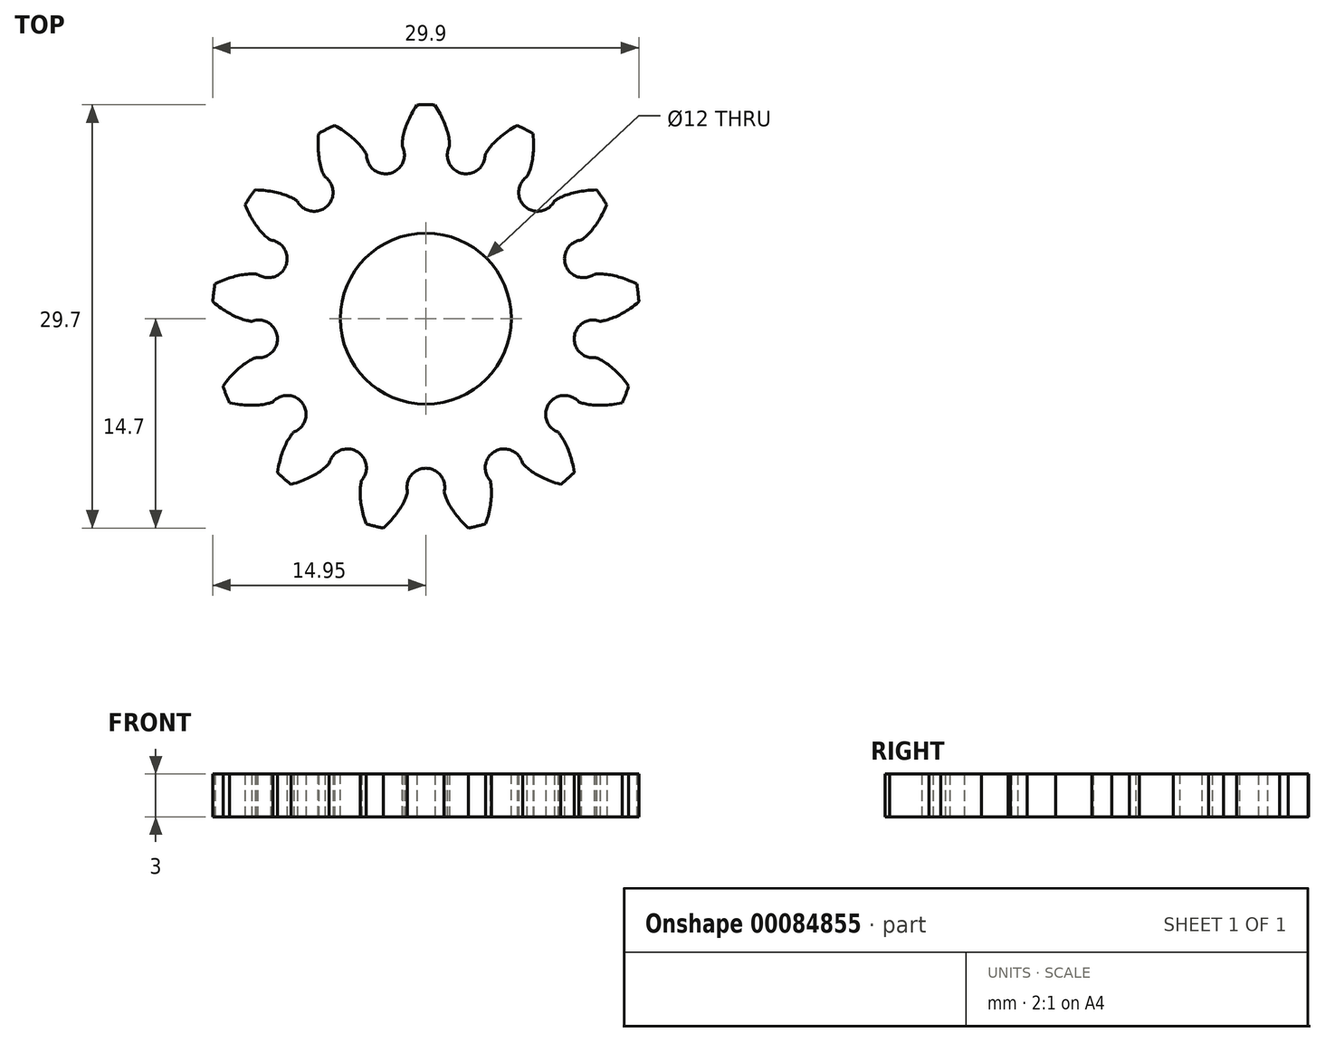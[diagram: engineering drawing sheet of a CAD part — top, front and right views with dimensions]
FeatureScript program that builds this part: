
annotation { "Feature Type Name" : "Feature", "Feature Type Description" : "" }
export const myFeature = defineFeature(function(context is Context, id is Id, definition is map)
    precondition{}
    {
        {
            assignVariable(context, id + "F0", {"name" : "Z", "anyValue" : 13});
        }
        {
            assignVariable(context, id + "F1", {"name" : "e", "anyValue" : 3});
        }
        {
            var Q0;
            Q0=qCreatedBy(makeId("Top.planeOp"),FACE);
            var sketch = newSketch(context, id + "F2", { "sketchPlane" : qUnion([Q0])});
            skCircle(sketch, "E0", {"center": v(0, 0) * mm, "radius": 13 * mm, "construction": true});
            skCircle(sketch, "E1", {"center": v(0, 0) * mm, "radius": 15 * mm, "construction": true});
            skLineSegment(sketch, "E2", {"start": v(-8.95, 13) * mm, "end": v(8.95, 13) * mm, "construction": true});
            skLineSegment(sketch, "E3", {"start": v(0, 0) * mm, "end": v(0, 13) * mm, "construction": true});
            skLineSegment(sketch, "E4", {"start": v(-4.18, 11.48) * mm, "end": v(0, 13) * mm, "construction": true});
            skLineSegment(sketch, "E5", {"start": v(0, 0) * mm, "end": v(-4.18, 11.48) * mm, "construction": true});
            skCircle(sketch, "E6", {"center": v(0, 0) * mm, "radius": 12.22 * mm, "construction": true});
            skLineSegment(sketch, "E7", {"start": v(-1.66, 12.1) * mm, "end": v(0.52, 12.2) * mm, "construction": true});
            skLineSegment(sketch, "E8", {"start": v(0.52, 12.2) * mm, "end": v(2.67, 11.92) * mm, "construction": true});
            skLineSegment(sketch, "E9", {"start": v(2.67, 11.92) * mm, "end": v(4.75, 11.26) * mm, "construction": true});
            skLineSegment(sketch, "E10", {"start": v(4.75, 11.26) * mm, "end": v(6.67, 10.24) * mm, "construction": true});
            skLineSegment(sketch, "E11", {"start": v(0.52, 12.2) * mm, "end": v(-1.66, 12.3) * mm, "construction": true});
            skLineSegment(sketch, "E12", {"start": v(4.75, 11.26) * mm, "end": v(2.74, 12.1) * mm, "construction": true});
            skLineSegment(sketch, "E13", {"start": v(2.74, 12.1) * mm, "end": v(0.73, 12.95) * mm, "construction": true});
            skLineSegment(sketch, "E14", {"start": v(0.73, 12.95) * mm, "end": v(-1.27, 13.8) * mm, "construction": true});
            skLineSegment(sketch, "E15", {"start": v(6.67, 10.24) * mm, "end": v(4.84, 11.42) * mm, "construction": true});
            skLineSegment(sketch, "E16", {"start": v(4.84, 11.42) * mm, "end": v(3.02, 12.61) * mm, "construction": true});
            skLineSegment(sketch, "E17", {"start": v(3.02, 12.61) * mm, "end": v(1.2, 13.8) * mm, "construction": true});
            skLineSegment(sketch, "E18", {"start": v(1.2, 13.8) * mm, "end": v(-0.63, 14.99) * mm, "construction": true});
            skLineSegment(sketch, "E19", {"start": v(2.67, 11.92) * mm, "end": v(0.55, 12.4) * mm, "construction": true});
            skLineSegment(sketch, "E20", {"start": v(0.55, 12.4) * mm, "end": v(-1.57, 12.87) * mm, "construction": true});
            skLineSegment(sketch, "E21", {"start": v(0, 0) * mm, "end": v(-1.66, 12.1) * mm, "construction": true});
            skFitSpline(sketch, "E22", {"points": [v(-1.66, 12.1) * mm, v(-1.66, 12.3) * mm, v(-1.57, 12.87) * mm, v(-1.27, 13.8) * mm, v(-0.63, 14.99) * mm], "startDerivative": vector(-0.22, 1.58) * mm, "endDerivative": vector(2.73, 4.2) * mm});
            skLineSegment(sketch, "E23", {"start": v(-0.63, 14.99) * mm, "end": v(-2.62, 11.93) * mm, "construction": true});
            skFitSpline(sketch, "E24.MirrorCS", {"points": [v(1.66, 12.1) * mm, v(1.66, 12.3) * mm, v(1.57, 12.87) * mm, v(1.27, 13.8) * mm, v(0.63, 14.99) * mm], "startDerivative": vector(0.22, 1.58) * mm, "endDerivative": vector(-2.73, 4.2) * mm});
            skArc(sketch, "E25", {"start": v(0.63, 14.99) * mm, "mid": v(0, 15) * mm, "end": v(-0.63, 14.99) * mm});
            skCircle(sketch, "E26", {"center": v(0, 0) * mm, "radius": 10.5 * mm, "construction": true});
            skLineSegment(sketch, "E27", {"start": v(0, 0) * mm, "end": v(-2.51, 10.2) * mm});
            skArc(sketch, "E28", {"start": v(-2.51, 10.2) * mm, "mid": v(-1.62, 10.94) * mm, "end": v(-1.66, 12.1) * mm});
            skArc(sketch, "E29.MirrorCS", {"start": v(2.51, 10.2) * mm, "mid": v(1.62, 10.94) * mm, "end": v(1.66, 12.1) * mm});
            skLineSegment(sketch, "E30.MirrorCS", {"start": v(0, 0) * mm, "end": v(2.51, 10.2) * mm});
            skArc(sketch, "E31", {"start": v(1.57, 12.9) * mm, "mid": v(0, 13) * mm, "end": v(-1.57, 12.9) * mm, "construction": true});
            skSolve(sketch);
        }
        {
            var Q0;
            Q0=makeQuery(id+"F2.imprint","IMPRINT",FACE,{"disambiguationData":[TD([[makeQuery(id+"F2.imprint","IMPRINT",EDGE,{"derivedFrom":sQuery(id+"F2.wireOp",EDGE,"E22")}),-1.0]])]});
            extrude(context, id + "F3", {"entities" : qUnion([Q0]), "endBound" : BoundingType.SYMMETRIC, "depth" : (getVariable(context, 'e')) * mm});
        }
        {
            var Q0;
            Q0=makeQuery(id+"F3.opExtrude","SWEPT_BODY",BODY,{"disambiguationData":[OSD([sQuery(id+"F2.wireOp",EDGE,"E22"),sQuery(id+"F2.wireOp",EDGE,"E24.MirrorCS"),sQuery(id+"F2.wireOp",EDGE,"E25"),sQuery(id+"F2.wireOp",EDGE,"E27"),sQuery(id+"F2.wireOp",EDGE,"E28"),sQuery(id+"F2.wireOp",EDGE,"E29.MirrorCS"),sQuery(id+"F2.wireOp",EDGE,"E30.MirrorCS")])]});
            var Q1;
            Q1=makeQuery(id+"F3.opExtrude","SWEPT_EDGE",EDGE,{"disambiguationData":[OSD([sQuery(id+"F2.wireOp",EDGE,"E27"),sQuery(id+"F2.wireOp",EDGE,"E30.MirrorCS")])]});
            circularPattern(context, id + "F4", {"operationType" : NewBodyOperationType.ADD, "entities" : qUnion([Q0]), "axis" : qUnion([Q1]), "angle" : 360 * degree, "instanceCount" : getVariable(context, 'Z'), "equalSpace" : true});
        }
        {
            var Q0;
            {var subQ0=makeQuery(id+"F3.opExtrude","CAP_FACE",FACE,{"disambiguationData":[OSD([sQuery(id+"F2.wireOp",EDGE,"E22"),sQuery(id+"F2.wireOp",EDGE,"E24.MirrorCS"),sQuery(id+"F2.wireOp",EDGE,"E25"),sQuery(id+"F2.wireOp",EDGE,"E27"),sQuery(id+"F2.wireOp",EDGE,"E28"),sQuery(id+"F2.wireOp",EDGE,"E29.MirrorCS"),sQuery(id+"F2.wireOp",EDGE,"E30.MirrorCS")])],"isStart":false});Q0=makeQuery(id+"F4.boolean.opBoolean","MERGE",FACE,{"derivedFrom":[subQ0,makeQuery(id+"F4.opPattern","COPY",FACE,{"derivedFrom":subQ0,"instanceName":"1"}),makeQuery(id+"F4.opPattern","COPY",FACE,{"derivedFrom":subQ0,"instanceName":"2"}),makeQuery(id+"F4.opPattern","COPY",FACE,{"derivedFrom":subQ0,"instanceName":"3"}),makeQuery(id+"F4.opPattern","COPY",FACE,{"derivedFrom":subQ0,"instanceName":"4"}),makeQuery(id+"F4.opPattern","COPY",FACE,{"derivedFrom":subQ0,"instanceName":"5"}),makeQuery(id+"F4.opPattern","COPY",FACE,{"derivedFrom":subQ0,"instanceName":"6"}),makeQuery(id+"F4.opPattern","COPY",FACE,{"derivedFrom":subQ0,"instanceName":"7"}),makeQuery(id+"F4.opPattern","COPY",FACE,{"derivedFrom":subQ0,"instanceName":"8"}),makeQuery(id+"F4.opPattern","COPY",FACE,{"derivedFrom":subQ0,"instanceName":"9"}),makeQuery(id+"F4.opPattern","COPY",FACE,{"derivedFrom":subQ0,"instanceName":"10"}),makeQuery(id+"F4.opPattern","COPY",FACE,{"derivedFrom":subQ0,"instanceName":"11"}),makeQuery(id+"F4.opPattern","COPY",FACE,{"derivedFrom":subQ0,"instanceName":"12"}),makeQuery(id+"F4.opPattern","COPY",FACE,{"derivedFrom":subQ0,"instanceName":"13"}),makeQuery(id+"F4.opPattern","COPY",FACE,{"derivedFrom":subQ0,"instanceName":"14"}),makeQuery(id+"F4.opPattern","COPY",FACE,{"derivedFrom":subQ0,"instanceName":"15"}),makeQuery(id+"F4.opPattern","COPY",FACE,{"derivedFrom":subQ0,"instanceName":"16"}),makeQuery(id+"F4.opPattern","COPY",FACE,{"derivedFrom":subQ0,"instanceName":"17"}),makeQuery(id+"F4.opPattern","COPY",FACE,{"derivedFrom":subQ0,"instanceName":"18"}),makeQuery(id+"F4.opPattern","COPY",FACE,{"derivedFrom":subQ0,"instanceName":"19"}),makeQuery(id+"F4.opPattern","COPY",FACE,{"derivedFrom":subQ0,"instanceName":"20"}),makeQuery(id+"F4.opPattern","COPY",FACE,{"derivedFrom":subQ0,"instanceName":"21"}),makeQuery(id+"F4.opPattern","COPY",FACE,{"derivedFrom":subQ0,"instanceName":"22"}),makeQuery(id+"F4.opPattern","COPY",FACE,{"derivedFrom":subQ0,"instanceName":"23"}),makeQuery(id+"F4.opPattern","COPY",FACE,{"derivedFrom":subQ0,"instanceName":"24"}),makeQuery(id+"F4.opPattern","COPY",FACE,{"derivedFrom":subQ0,"instanceName":"25"})]});}
            var sketch = newSketch(context, id + "F5", { "sketchPlane" : qUnion([Q0])});
            skCircle(sketch, "E32", {"center": v(0, 0) * mm, "radius": 6 * mm});
            skSolve(sketch);
        }
        {
            var Q0;
            Q0=qSketchRegion(id+"F5",true);
            extrude(context, id + "F6", {"entities" : qUnion([Q0]), "operationType" : NewBodyOperationType.REMOVE, "endBound" : BoundingType.THROUGH_ALL, "oppositeDirection" : true, "depth" : 25 * mm});
        }
    });
